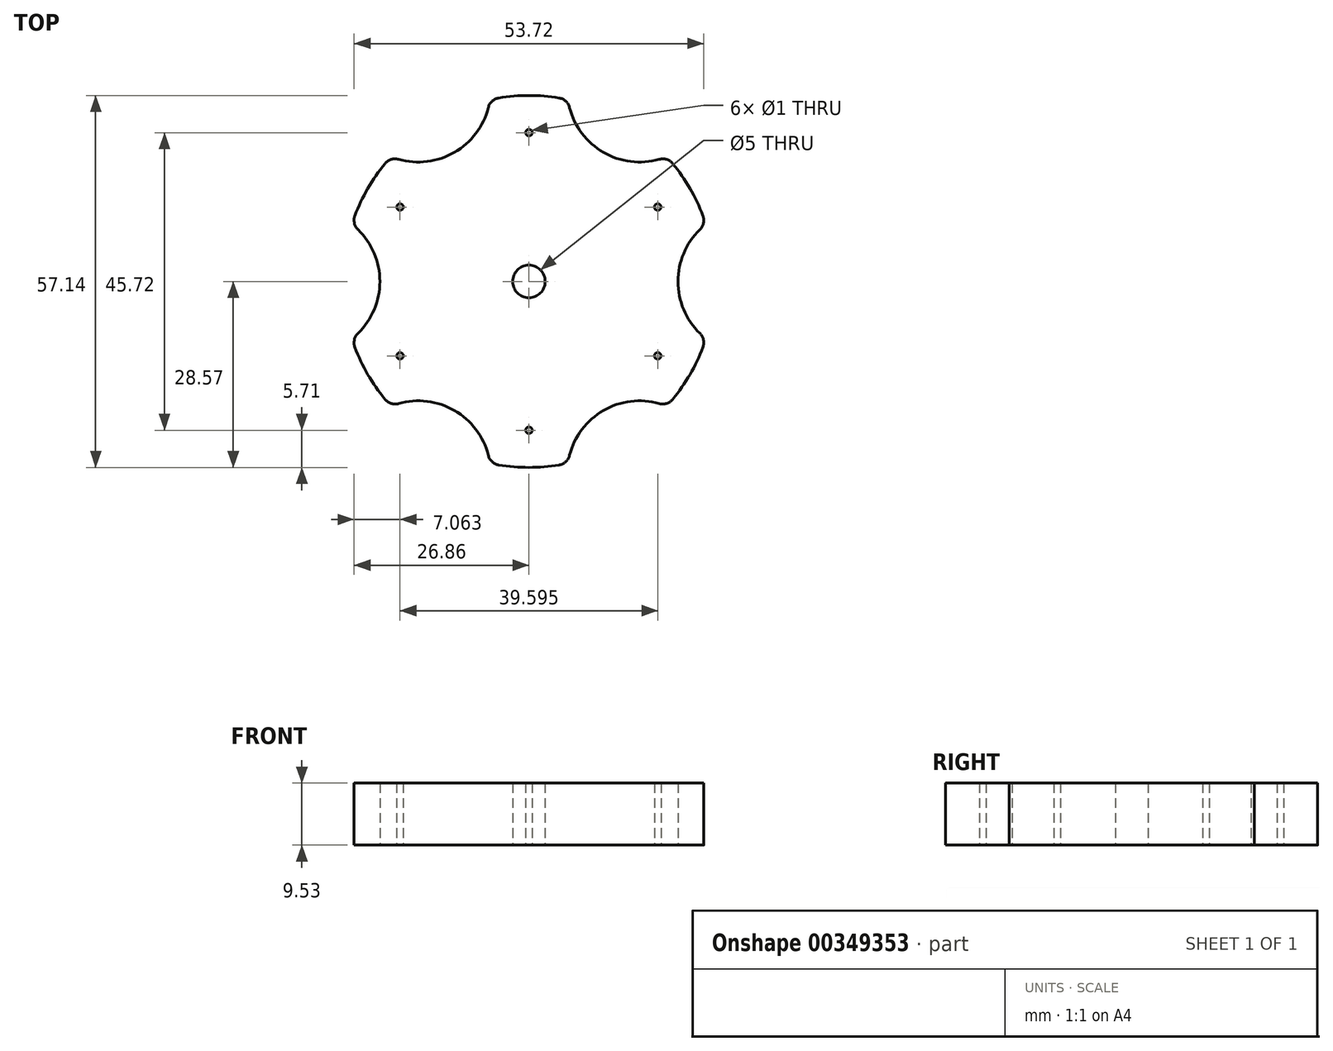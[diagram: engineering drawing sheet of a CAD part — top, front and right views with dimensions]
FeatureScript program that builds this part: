
annotation { "Feature Type Name" : "Feature", "Feature Type Description" : "" }
export const myFeature = defineFeature(function(context is Context, id is Id, definition is map)
    precondition{}
    {
        {
            var Q0;
            Q0=qCreatedBy(makeId("Top.planeOp"),FACE);
            var sketch = newSketch(context, id + "F0", { "sketchPlane" : qUnion([Q0])});
            skCircle(sketch, "E0", {"center": v(0, 0) * mm, "radius": 28.58 * mm});
            skCircle(sketch, "E1", {"center": v(0, 0) * mm, "radius": 2.5 * mm});
            skSolve(sketch);
        }
        {
            var Q0;
            Q0=makeQuery(id+"F0.imprint","IMPRINT",FACE,{"disambiguationData":[TD([[makeQuery(id+"F0.imprint","IMPRINT",EDGE,{"derivedFrom":sQuery(id+"F0.wireOp",EDGE,"E0")}),1.0]])]});
            extrude(context, id + "F1", {"entities" : qUnion([Q0]), "depth" : 9.52 * mm});
        }
        {
            var Q0;
            Q0=qCreatedBy(makeId("Top.planeOp"),FACE);
            var sketch = newSketch(context, id + "F2", { "sketchPlane" : qUnion([Q0])});
            skCircle(sketch, "E2", {"center": v(0, 0) * mm, "radius": 34.01 * mm});
            skCircle(sketch, "E3", {"center": v(-34.01, 0) * mm, "radius": 11.11 * mm});
            skCircle(sketch, "E4.1.0", {"center": v(-17, -29.45) * mm, "radius": 11.11 * mm});
            skCircle(sketch, "E4.2.0", {"center": v(17, -29.45) * mm, "radius": 11.11 * mm});
            skCircle(sketch, "E4.3.0", {"center": v(34.01, 0) * mm, "radius": 11.11 * mm});
            skCircle(sketch, "E4.4.0", {"center": v(17, 29.45) * mm, "radius": 11.11 * mm});
            skCircle(sketch, "E4.5.0", {"center": v(-17, 29.45) * mm, "radius": 11.11 * mm});
            skSolve(sketch);
        }
        {
            var Q0;
            {var subQ0=sQuery(id+"F2.wireOp",EDGE,"E4.2.0");var subQ1=sQuery(id+"F2.wireOp",EDGE,"E2");var subQ2=makeQuery(id+"F2.imprint","INTERSECT",VERTEX,{"disambiguationData":[OD(0.0)],"derivedFrom":[subQ1,subQ0]});Q0=makeQuery(id+"F2.imprint","IMPRINT",FACE,{"disambiguationData":[TD([[makeQuery(id+"F2.imprint","IMPRINT",EDGE,{"disambiguationData":[TD([[subQ2,-1.0]])],"derivedFrom":subQ1}),1.0]])]});}
            var Q1;
            {var subQ0=sQuery(id+"F2.wireOp",EDGE,"E4.1.0");var subQ1=sQuery(id+"F2.wireOp",EDGE,"E2");var subQ2=makeQuery(id+"F2.imprint","INTERSECT",VERTEX,{"disambiguationData":[OD(0.0)],"derivedFrom":[subQ1,subQ0]});Q1=makeQuery(id+"F2.imprint","IMPRINT",FACE,{"disambiguationData":[TD([[makeQuery(id+"F2.imprint","IMPRINT",EDGE,{"disambiguationData":[TD([[subQ2,-1.0]])],"derivedFrom":subQ1}),1.0]])]});}
            var Q2;
            {var subQ0=sQuery(id+"F2.wireOp",EDGE,"E3");var subQ1=sQuery(id+"F2.wireOp",EDGE,"E2");var subQ2=makeQuery(id+"F2.imprint","INTERSECT",VERTEX,{"disambiguationData":[OD(0.0)],"derivedFrom":[subQ1,subQ0]});Q2=makeQuery(id+"F2.imprint","IMPRINT",FACE,{"disambiguationData":[TD([[makeQuery(id+"F2.imprint","IMPRINT",EDGE,{"disambiguationData":[TD([[subQ2,-1.0]])],"derivedFrom":subQ1}),1.0]])]});}
            var Q3;
            {var subQ0=sQuery(id+"F2.wireOp",EDGE,"E4.5.0");var subQ1=sQuery(id+"F2.wireOp",EDGE,"E2");var subQ2=makeQuery(id+"F2.imprint","INTERSECT",VERTEX,{"disambiguationData":[OD(0.0)],"derivedFrom":[subQ1,subQ0]});Q3=makeQuery(id+"F2.imprint","IMPRINT",FACE,{"disambiguationData":[TD([[makeQuery(id+"F2.imprint","IMPRINT",EDGE,{"disambiguationData":[TD([[subQ2,-1.0]])],"derivedFrom":subQ1}),1.0]])]});}
            var Q4;
            {var subQ0=sQuery(id+"F2.wireOp",EDGE,"E4.4.0");var subQ1=sQuery(id+"F2.wireOp",EDGE,"E2");var subQ2=makeQuery(id+"F2.imprint","INTERSECT",VERTEX,{"disambiguationData":[OD(0.0)],"derivedFrom":[subQ1,subQ0]});Q4=makeQuery(id+"F2.imprint","IMPRINT",FACE,{"disambiguationData":[TD([[makeQuery(id+"F2.imprint","IMPRINT",EDGE,{"disambiguationData":[TD([[subQ2,-1.0]])],"derivedFrom":subQ1}),1.0]])]});}
            var Q5;
            {var subQ0=sQuery(id+"F2.wireOp",EDGE,"E4.3.0");var subQ1=sQuery(id+"F2.wireOp",EDGE,"E2");var subQ2=makeQuery(id+"F2.imprint","INTERSECT",VERTEX,{"disambiguationData":[OD(0.0)],"derivedFrom":[subQ1,subQ0]});Q5=makeQuery(id+"F2.imprint","IMPRINT",FACE,{"disambiguationData":[TD([[makeQuery(id+"F2.imprint","IMPRINT",EDGE,{"disambiguationData":[TD([[subQ2,1.0]])],"derivedFrom":subQ1}),1.0]])]});}
            extrude(context, id + "F3", {"entities" : qUnion([Q0, Q1, Q2, Q3, Q4, Q5]), "operationType" : NewBodyOperationType.REMOVE, "depth" : 25.4 * mm});
        }
        {
            var Q0;
            Q0=qCreatedBy(makeId("Top.planeOp"),FACE);
            var sketch = newSketch(context, id + "F4", { "sketchPlane" : qUnion([Q0])});
            skCircle(sketch, "E5", {"center": v(0, 22.86) * mm, "radius": 0.5 * mm});
            skCircle(sketch, "E6.1.0", {"center": v(-19.8, 11.43) * mm, "radius": 0.5 * mm});
            skCircle(sketch, "E6.2.0", {"center": v(-19.8, -11.43) * mm, "radius": 0.5 * mm});
            skCircle(sketch, "E6.3.0", {"center": v(0, -22.86) * mm, "radius": 0.5 * mm});
            skCircle(sketch, "E6.4.0", {"center": v(19.8, -11.43) * mm, "radius": 0.5 * mm});
            skCircle(sketch, "E6.5.0", {"center": v(19.8, 11.43) * mm, "radius": 0.5 * mm});
            skPoint(sketch, "E6.center", {"position": v(0, 0) * mm});
            skSolve(sketch);
        }
        {
            var Q0;
            Q0=qSketchRegion(id+"F4",true);
            extrude(context, id + "F5", {"entities" : qUnion([Q0]), "operationType" : NewBodyOperationType.REMOVE, "depth" : 25.4 * mm});
        }
        {
            var Q0;
            Q0=makeQuery(id+"F3.boolean.opBoolean","INTERSECT",EDGE,{"disambiguationData":[OD(1.0)],"derivedFrom":[makeQuery(id+"F1.opExtrude","SWEPT_FACE",FACE,{"disambiguationData":[OSD([sQuery(id+"F0.wireOp",EDGE,"E0")])]}),makeQuery(id+"F3.opExtrude","SWEPT_FACE",FACE,{"disambiguationData":[OSD([sQuery(id+"F2.wireOp",EDGE,"E4.5.0")])]})]});
            var Q1;
            Q1=makeQuery(id+"F3.boolean.opBoolean","INTERSECT",EDGE,{"disambiguationData":[OD(1.0)],"derivedFrom":[makeQuery(id+"F1.opExtrude","SWEPT_FACE",FACE,{"disambiguationData":[OSD([sQuery(id+"F0.wireOp",EDGE,"E0")])]}),makeQuery(id+"F3.opExtrude","SWEPT_FACE",FACE,{"disambiguationData":[OSD([sQuery(id+"F2.wireOp",EDGE,"E4.4.0")])]})]});
            var Q2;
            Q2=makeQuery(id+"F3.boolean.opBoolean","INTERSECT",EDGE,{"disambiguationData":[OD(0.0)],"derivedFrom":[makeQuery(id+"F1.opExtrude","SWEPT_FACE",FACE,{"disambiguationData":[OSD([sQuery(id+"F0.wireOp",EDGE,"E0")])]}),makeQuery(id+"F3.opExtrude","SWEPT_FACE",FACE,{"disambiguationData":[OSD([sQuery(id+"F2.wireOp",EDGE,"E4.4.0")])]})]});
            var Q3;
            Q3=makeQuery(id+"F3.boolean.opBoolean","INTERSECT",EDGE,{"disambiguationData":[OD(0.0)],"derivedFrom":[makeQuery(id+"F1.opExtrude","SWEPT_FACE",FACE,{"disambiguationData":[OSD([sQuery(id+"F0.wireOp",EDGE,"E0")])]}),makeQuery(id+"F3.opExtrude","SWEPT_FACE",FACE,{"disambiguationData":[OSD([sQuery(id+"F2.wireOp",EDGE,"E4.5.0")])]})]});
            var Q4;
            Q4=makeQuery(id+"F3.boolean.opBoolean","INTERSECT",EDGE,{"disambiguationData":[OD(1.0)],"derivedFrom":[makeQuery(id+"F1.opExtrude","SWEPT_FACE",FACE,{"disambiguationData":[OSD([sQuery(id+"F0.wireOp",EDGE,"E0")])]}),makeQuery(id+"F3.opExtrude","SWEPT_FACE",FACE,{"disambiguationData":[OSD([sQuery(id+"F2.wireOp",EDGE,"E3")])]})]});
            var Q5;
            Q5=makeQuery(id+"F3.boolean.opBoolean","INTERSECT",EDGE,{"disambiguationData":[OD(0.0)],"derivedFrom":[makeQuery(id+"F1.opExtrude","SWEPT_FACE",FACE,{"disambiguationData":[OSD([sQuery(id+"F0.wireOp",EDGE,"E0")])]}),makeQuery(id+"F3.opExtrude","SWEPT_FACE",FACE,{"disambiguationData":[OSD([sQuery(id+"F2.wireOp",EDGE,"E3")])]})]});
            var Q6;
            Q6=makeQuery(id+"F3.boolean.opBoolean","INTERSECT",EDGE,{"disambiguationData":[OD(0.0)],"derivedFrom":[makeQuery(id+"F1.opExtrude","SWEPT_FACE",FACE,{"disambiguationData":[OSD([sQuery(id+"F0.wireOp",EDGE,"E0")])]}),makeQuery(id+"F3.opExtrude","SWEPT_FACE",FACE,{"disambiguationData":[OSD([sQuery(id+"F2.wireOp",EDGE,"E4.1.0")])]})]});
            var Q7;
            Q7=makeQuery(id+"F3.boolean.opBoolean","INTERSECT",EDGE,{"disambiguationData":[OD(1.0)],"derivedFrom":[makeQuery(id+"F1.opExtrude","SWEPT_FACE",FACE,{"disambiguationData":[OSD([sQuery(id+"F0.wireOp",EDGE,"E0")])]}),makeQuery(id+"F3.opExtrude","SWEPT_FACE",FACE,{"disambiguationData":[OSD([sQuery(id+"F2.wireOp",EDGE,"E4.1.0")])]})]});
            var Q8;
            Q8=makeQuery(id+"F3.boolean.opBoolean","INTERSECT",EDGE,{"disambiguationData":[OD(0.0)],"derivedFrom":[makeQuery(id+"F1.opExtrude","SWEPT_FACE",FACE,{"disambiguationData":[OSD([sQuery(id+"F0.wireOp",EDGE,"E0")])]}),makeQuery(id+"F3.opExtrude","SWEPT_FACE",FACE,{"disambiguationData":[OSD([sQuery(id+"F2.wireOp",EDGE,"E4.2.0")])]})]});
            var Q9;
            Q9=makeQuery(id+"F3.boolean.opBoolean","INTERSECT",EDGE,{"disambiguationData":[OD(1.0)],"derivedFrom":[makeQuery(id+"F1.opExtrude","SWEPT_FACE",FACE,{"disambiguationData":[OSD([sQuery(id+"F0.wireOp",EDGE,"E0")])]}),makeQuery(id+"F3.opExtrude","SWEPT_FACE",FACE,{"disambiguationData":[OSD([sQuery(id+"F2.wireOp",EDGE,"E4.2.0")])]})]});
            var Q10;
            Q10=makeQuery(id+"F3.boolean.opBoolean","INTERSECT",EDGE,{"disambiguationData":[OD(0.0)],"derivedFrom":[makeQuery(id+"F1.opExtrude","SWEPT_FACE",FACE,{"disambiguationData":[OSD([sQuery(id+"F0.wireOp",EDGE,"E0")])]}),makeQuery(id+"F3.opExtrude","SWEPT_FACE",FACE,{"disambiguationData":[OSD([sQuery(id+"F2.wireOp",EDGE,"E4.3.0")])]})]});
            var Q11;
            Q11=makeQuery(id+"F3.boolean.opBoolean","INTERSECT",EDGE,{"disambiguationData":[OD(1.0)],"derivedFrom":[makeQuery(id+"F1.opExtrude","SWEPT_FACE",FACE,{"disambiguationData":[OSD([sQuery(id+"F0.wireOp",EDGE,"E0")])]}),makeQuery(id+"F3.opExtrude","SWEPT_FACE",FACE,{"disambiguationData":[OSD([sQuery(id+"F2.wireOp",EDGE,"E4.3.0")])]})]});
            fillet(context, id + "F6", {"entities" : qUnion([Q0, Q1, Q2, Q3, Q4, Q5, Q6, Q7, Q8, Q9, Q10, Q11]), "radius" : 2 * mm, "tangentPropagation" : true, "allowEdgeOverflow" : false});
        }
    });
